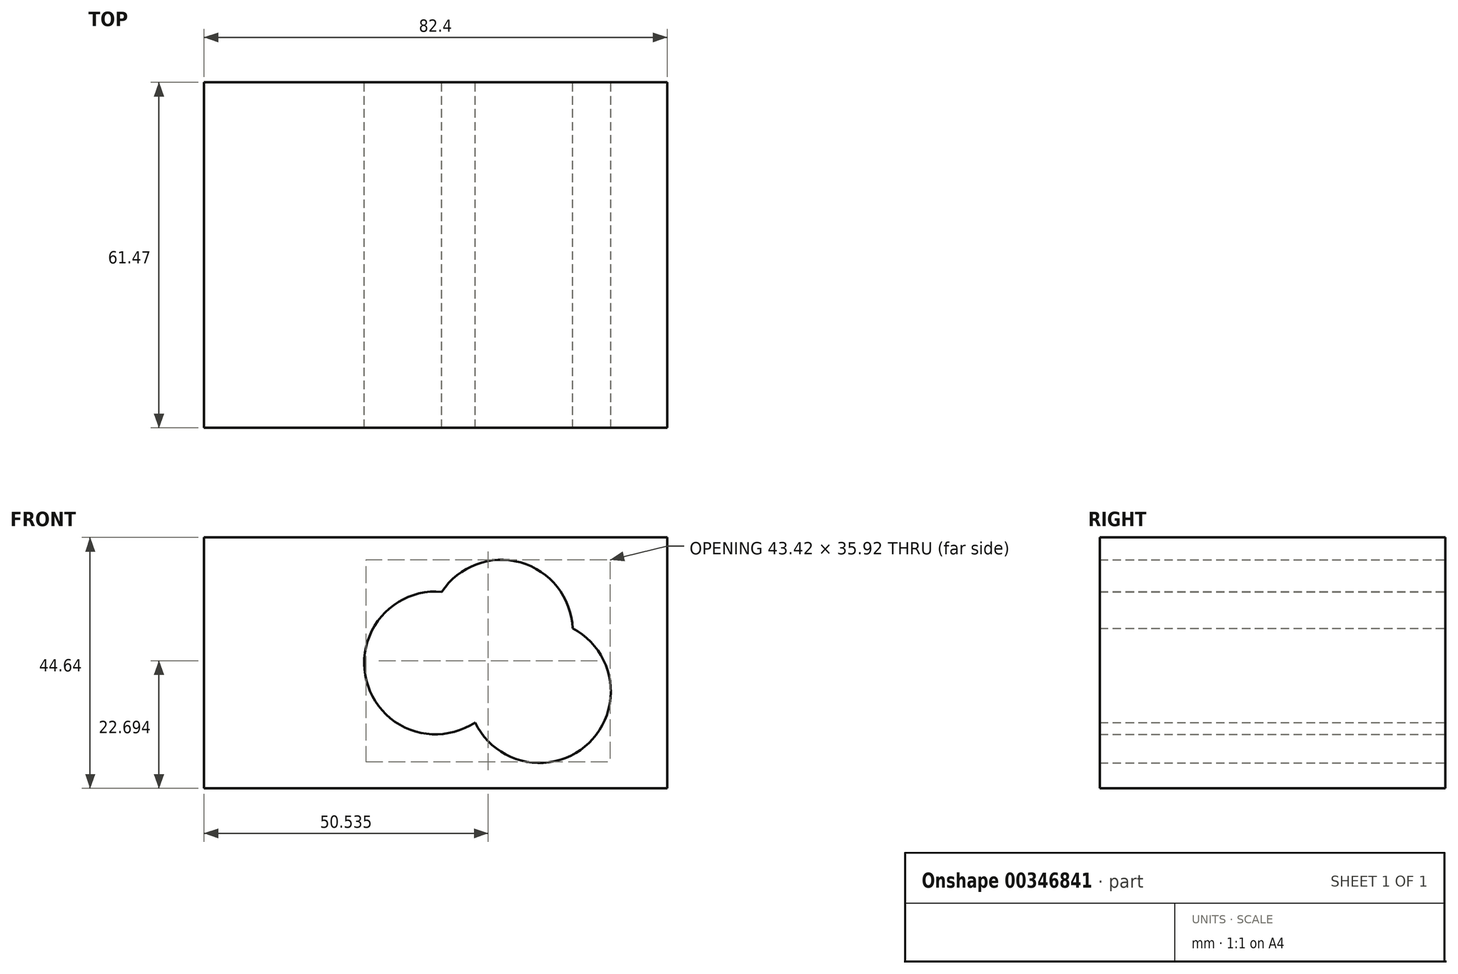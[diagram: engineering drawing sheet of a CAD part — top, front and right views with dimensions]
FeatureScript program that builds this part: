
annotation { "Feature Type Name" : "Feature", "Feature Type Description" : "" }
export const myFeature = defineFeature(function(context is Context, id is Id, definition is map)
    precondition{}
    {
        {
            var Q0;
            Q0=qCreatedBy(makeId("Front.planeOp"),FACE);
            var sketch = newSketch(context, id + "F0", { "sketchPlane" : qUnion([Q0])});
            skLineSegment(sketch, "E0.bottom", {"start": v(-41.2, 22.32) * mm, "end": v(41.2, 22.32) * mm});
            skLineSegment(sketch, "E0.top", {"start": v(-41.2, -22.32) * mm, "end": v(41.2, -22.32) * mm});
            skLineSegment(sketch, "E0.left", {"start": v(-41.2, 22.32) * mm, "end": v(-41.2, -22.32) * mm});
            skLineSegment(sketch, "E0.right", {"start": v(41.2, 22.32) * mm, "end": v(41.2, -22.32) * mm});
            skPoint(sketch, "E0.middle", {"position": v(0, 0) * mm});
            skCircle(sketch, "E1", {"center": v(0, 0) * mm, "radius": 12.7 * mm});
            skCircle(sketch, "E2", {"center": v(11.69, 5.65) * mm, "radius": 12.7 * mm});
            skCircle(sketch, "E3", {"center": v(18.47, -5.09) * mm, "radius": 12.7 * mm});
            skSolve(sketch);
        }
        {
            var Q0;
            Q0 = qSketchRegion(id + "F0", true);
            extrude(context, id + "F1", {"entities" : qUnion([Q0]), "depth" : 61.47 * mm, "offsetDistance" : 25.4 * mm});
        }
    });
